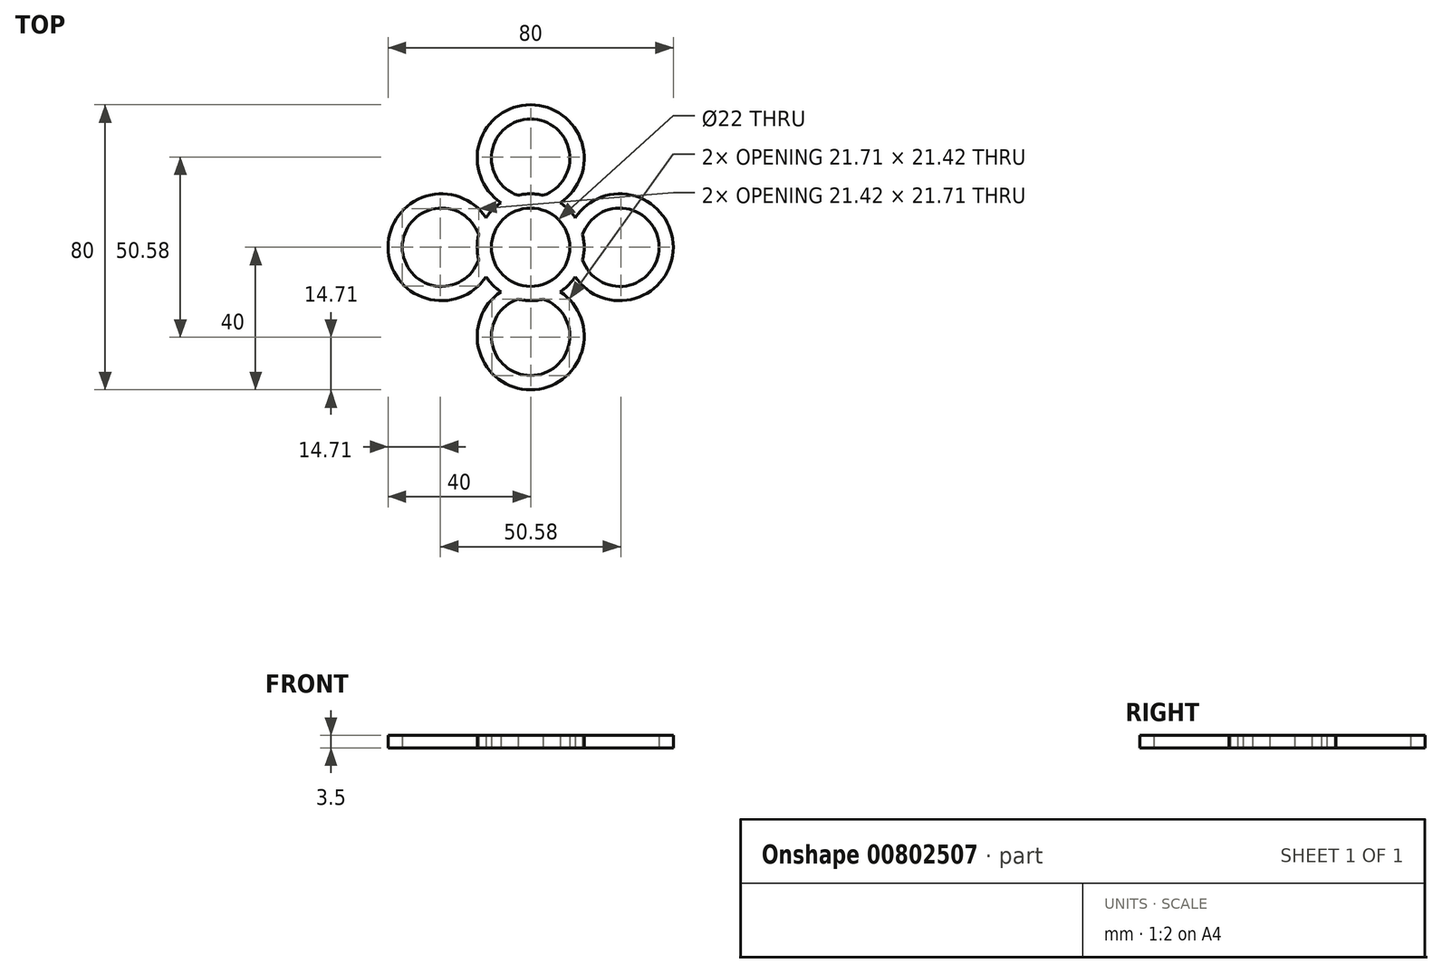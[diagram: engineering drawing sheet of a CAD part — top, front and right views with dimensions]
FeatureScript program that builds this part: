
annotation { "Feature Type Name" : "Feature", "Feature Type Description" : "" }
export const myFeature = defineFeature(function(context is Context, id is Id, definition is map)
    precondition{}
    {
        {
            var Q0;
            Q0=qCreatedBy(makeId("Top.planeOp"),FACE);
            var sketch = newSketch(context, id + "F0", { "sketchPlane" : qUnion([Q0])});
            skCircle(sketch, "E0", {"center": v(0, 0) * mm, "radius": 11 * mm});
            skArc(sketch, "E1", {"start": v(-8.3, 12.5) * mm, "mid": v(-10.6, 10.6) * mm, "end": v(-12.5, 8.3) * mm});
            skLineSegment(sketch, "E2", {"start": v(0, 11) * mm, "end": v(0, 25) * mm});
            skArc(sketch, "E3", {"start": v(3.52, 14.58) * mm, "mid": v(0, 36) * mm, "end": v(-3.52, 14.58) * mm});
            skArc(sketch, "E4.trimOffspring", {"start": v(8.3, 12.5) * mm, "mid": v(0, 40) * mm, "end": v(-8.3, 12.5) * mm});
            skArc(sketch, "E5.trimOffspring", {"start": v(3.52, 14.58) * mm, "mid": v(0, 15) * mm, "end": v(-3.52, 14.58) * mm});
            skArc(sketch, "E6.1.0", {"start": v(-12.5, 8.3) * mm, "mid": v(-40, 0) * mm, "end": v(-12.5, -8.3) * mm});
            skArc(sketch, "E6.1.1", {"start": v(-14.58, 3.52) * mm, "mid": v(-36, 0) * mm, "end": v(-14.58, -3.52) * mm});
            skArc(sketch, "E6.2.0", {"start": v(-8.3, -12.5) * mm, "mid": v(0, -40) * mm, "end": v(8.3, -12.5) * mm});
            skArc(sketch, "E6.2.1", {"start": v(-3.52, -14.58) * mm, "mid": v(0, -36) * mm, "end": v(3.52, -14.58) * mm});
            skArc(sketch, "E6.2.2", {"start": v(-3.52, -14.58) * mm, "mid": v(0, -15) * mm, "end": v(3.52, -14.58) * mm});
            skArc(sketch, "E6.3.0", {"start": v(12.5, -8.3) * mm, "mid": v(40, 0) * mm, "end": v(12.5, 8.3) * mm});
            skArc(sketch, "E6.3.1", {"start": v(14.58, -3.52) * mm, "mid": v(36, 0) * mm, "end": v(14.58, 3.52) * mm});
            skArc(sketch, "E6.3.2", {"start": v(14.58, -3.52) * mm, "mid": v(15, 0) * mm, "end": v(14.58, 3.52) * mm});
            skArc(sketch, "E7.trimOffspring", {"start": v(-14.58, 3.52) * mm, "mid": v(-15, 0) * mm, "end": v(-14.58, -3.52) * mm});
            skArc(sketch, "E8.trimOffspring", {"start": v(12.5, 8.3) * mm, "mid": v(10.6, 10.6) * mm, "end": v(8.3, 12.5) * mm});
            skArc(sketch, "E9.trimOffspring", {"start": v(8.3, -12.5) * mm, "mid": v(10.6, -10.6) * mm, "end": v(12.5, -8.3) * mm});
            skArc(sketch, "E10.trimOffspring", {"start": v(-12.5, -8.3) * mm, "mid": v(-10.6, -10.6) * mm, "end": v(-8.3, -12.5) * mm});
            skSolve(sketch);
        }
        {
            var Q0;
            Q0=makeQuery(id+"F0.imprint","IMPRINT",FACE,{"disambiguationData":[TD([[makeQuery(id+"F0.imprint","IMPRINT",EDGE,{"derivedFrom":sQuery(id+"F0.wireOp",EDGE,"E0")}),-1.0]])]});
            extrude(context, id + "F1", {"entities" : qUnion([Q0]), "depth" : 3.5 * mm, "offsetDistance" : 25 * mm});
        }
    });
